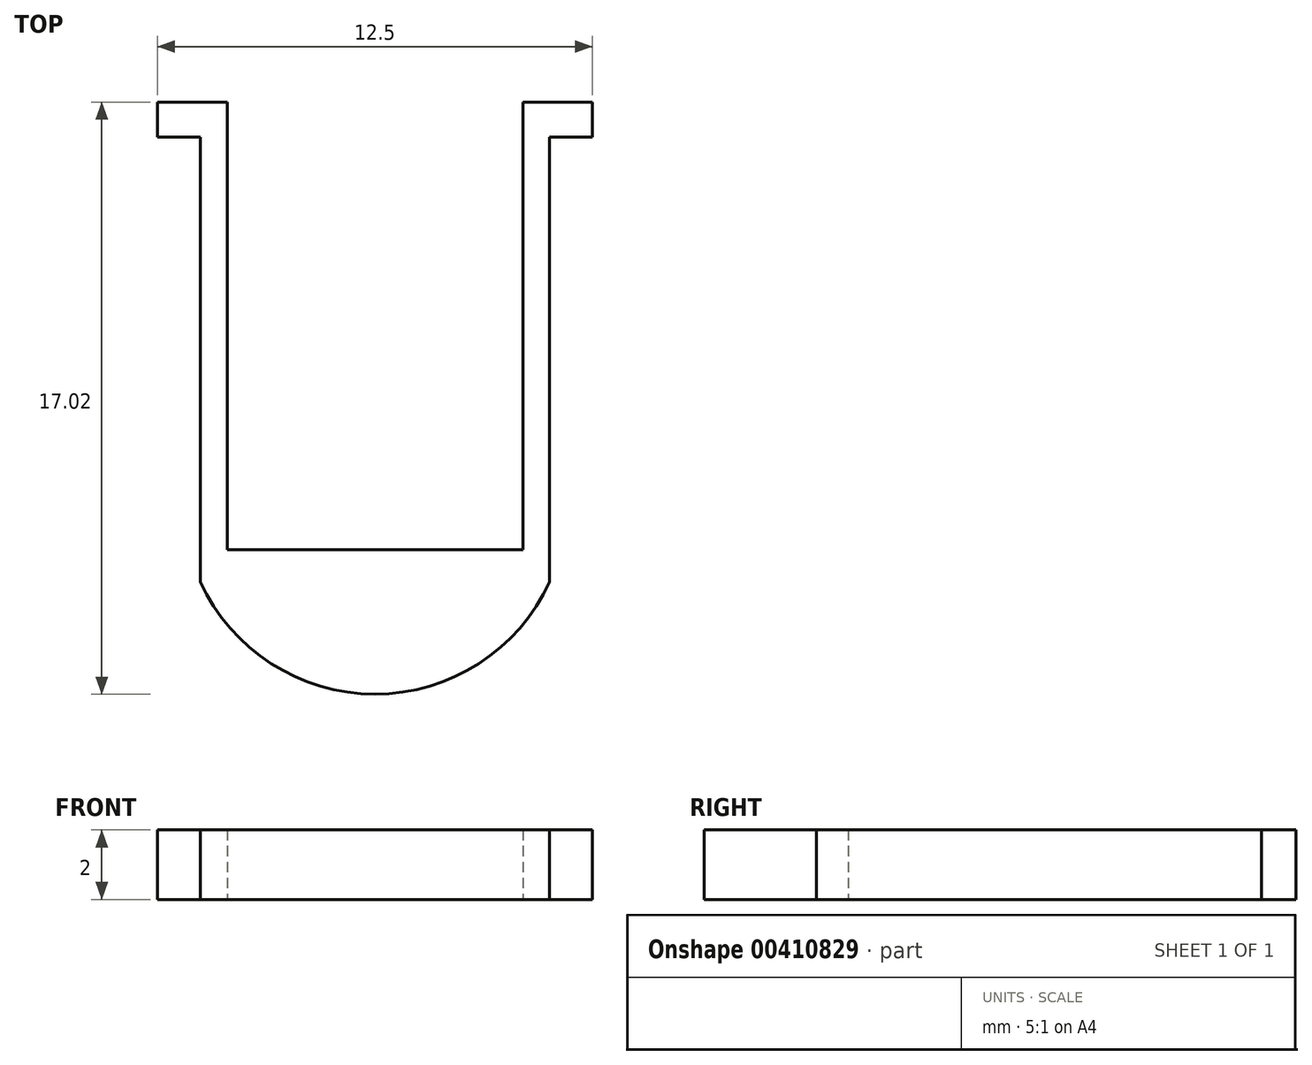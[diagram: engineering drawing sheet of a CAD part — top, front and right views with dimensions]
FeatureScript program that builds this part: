
annotation { "Feature Type Name" : "Feature", "Feature Type Description" : "" }
export const myFeature = defineFeature(function(context is Context, id is Id, definition is map)
    precondition{}
    {
        {
            var Q0;
            Q0=qCreatedBy(makeId("Top.planeOp"),FACE);
            var sketch = newSketch(context, id + "F0", { "sketchPlane" : qUnion([Q0])});
            skLineSegment(sketch, "E0.0", {"start": v(-4.25, 0) * mm, "end": v(-4.25, -12.87) * mm});
            skLineSegment(sketch, "E1.0", {"start": v(4.25, 0) * mm, "end": v(4.25, -12.87) * mm});
            skLineSegment(sketch, "E2.0", {"start": v(5.02, -1) * mm, "end": v(5.02, -13.79) * mm});
            skLineSegment(sketch, "E3.0", {"start": v(-5.02, -1) * mm, "end": v(-5.02, -13.79) * mm});
            skLineSegment(sketch, "E4", {"start": v(-6.25, 0) * mm, "end": v(-4.25, 0) * mm});
            skPoint(sketch, "E4.startSnap0", {"position": v(-5.02, 0) * mm});
            skLineSegment(sketch, "E5.0", {"start": v(-6.25, -1) * mm, "end": v(-5.02, -1) * mm});
            skLineSegment(sketch, "E6", {"start": v(-6.25, 0) * mm, "end": v(-6.25, -1) * mm});
            skLineSegment(sketch, "E7", {"start": v(6.25, 0) * mm, "end": v(6.25, -1) * mm});
            skPoint(sketch, "E8.orphan", {"position": v(-5.02, 4.25) * mm});
            skLineSegment(sketch, "E9.trimOffspring", {"start": v(5.02, -1) * mm, "end": v(6.25, -1) * mm});
            skLineSegment(sketch, "E10.trimOffspring", {"start": v(4.25, 0) * mm, "end": v(6.25, 0) * mm});
            skPoint(sketch, "E11.orphan", {"position": v(-5.02, -4.25) * mm});
            skLineSegment(sketch, "E12", {"start": v(-4.25, -12.87) * mm, "end": v(4.25, -12.87) * mm});
            skArc(sketch, "E13", {"start": v(-5.02, -13.79) * mm, "mid": v(0, -17.02) * mm, "end": v(5.02, -13.79) * mm});
            skSolve(sketch);
        }
        {
            var Q0;
            Q0 = qSketchRegion(id + "F0", true);
            extrude(context, id + "F1", {"entities" : qUnion([Q0]), "depth" : 2 * mm});
        }
    });
